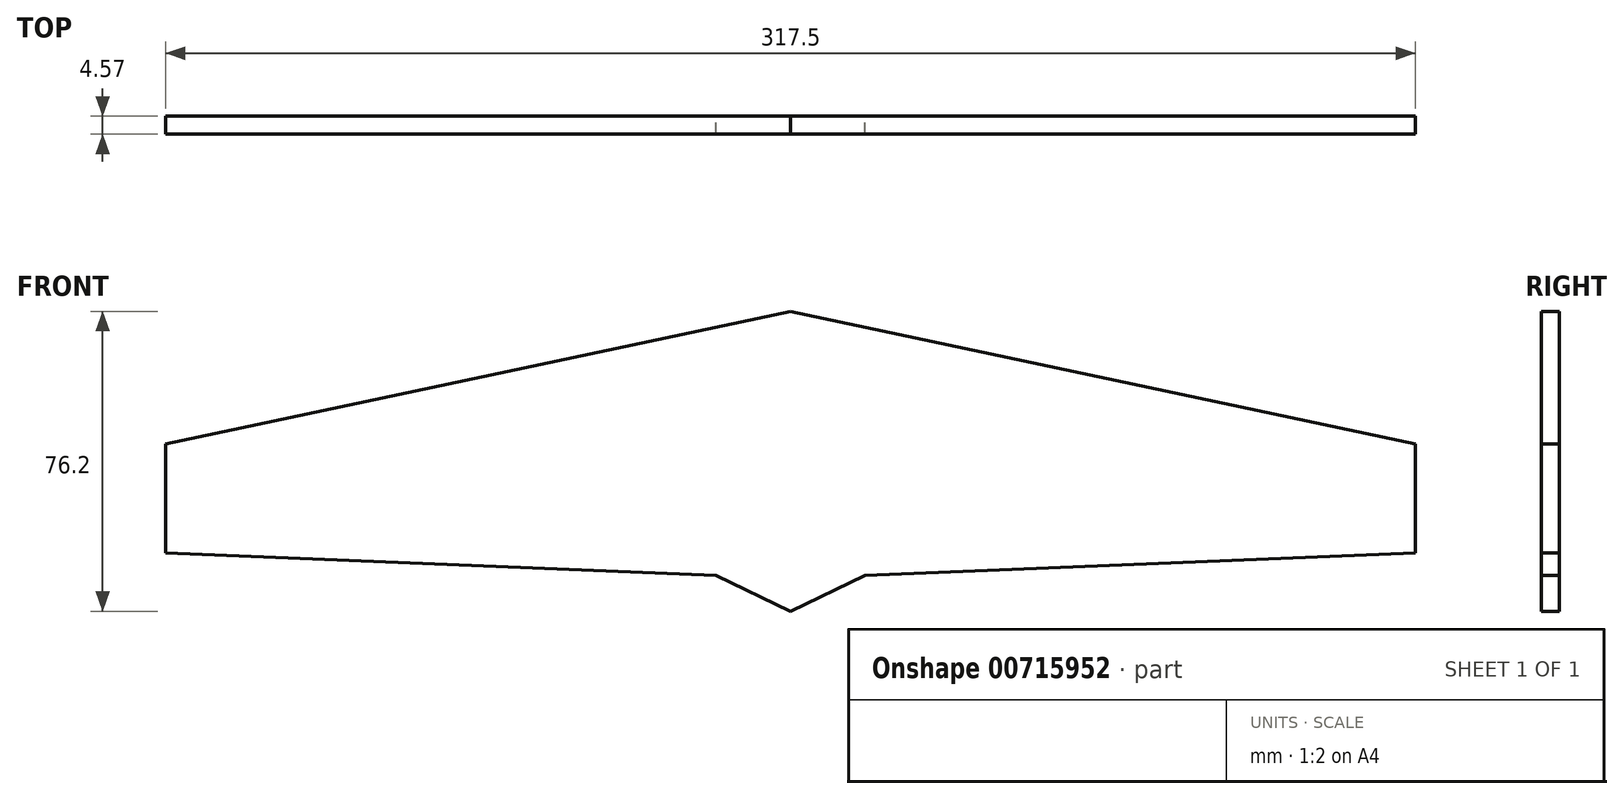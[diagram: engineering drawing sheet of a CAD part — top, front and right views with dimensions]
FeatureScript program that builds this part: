
annotation { "Feature Type Name" : "Feature", "Feature Type Description" : "" }
export const myFeature = defineFeature(function(context is Context, id is Id, definition is map)
    precondition{}
    {
        {
            var Q0;
            Q0=qCreatedBy(makeId("Front.planeOp"),FACE);
            var sketch = newSketch(context, id + "F0", { "sketchPlane" : qUnion([Q0])});
            skLineSegment(sketch, "E0.bottom", {"start": v(0, 0) * mm, "end": v(317.5, 0) * mm});
            skLineSegment(sketch, "E0.top", {"start": v(0, 76.2) * mm, "end": v(317.5, 76.2) * mm});
            skLineSegment(sketch, "E0.left", {"start": v(0, 0) * mm, "end": v(0, 76.2) * mm});
            skLineSegment(sketch, "E0.right", {"start": v(317.5, 0) * mm, "end": v(317.5, 76.2) * mm});
            skLineSegment(sketch, "E1", {"start": v(158.75, 76.2) * mm, "end": v(0, 42.45) * mm});
            skLineSegment(sketch, "E2", {"start": v(0, 42.45) * mm, "end": v(0, 14.84) * mm});
            skLineSegment(sketch, "E3", {"start": v(0, 14.84) * mm, "end": v(139.77, 9.16) * mm});
            skLineSegment(sketch, "E4", {"start": v(139.77, 9.16) * mm, "end": v(158.75, 0) * mm});
            skLineSegment(sketch, "E5", {"start": v(158.75, 0) * mm, "end": v(158.75, 76.2) * mm});
            skLineSegment(sketch, "E6.MirrorCS", {"start": v(158.75, 76.2) * mm, "end": v(317.5, 42.45) * mm});
            skLineSegment(sketch, "E7.MirrorCS", {"start": v(317.5, 42.45) * mm, "end": v(317.5, 14.84) * mm});
            skLineSegment(sketch, "E8.MirrorCS", {"start": v(317.5, 14.84) * mm, "end": v(177.73, 9.16) * mm});
            skLineSegment(sketch, "E9.MirrorCS", {"start": v(177.73, 9.16) * mm, "end": v(158.75, 0) * mm});
            skSolve(sketch);
        }
        {
            var Q0;
            Q0=makeQuery(id+"F0.imprint","IMPRINT",FACE,{"disambiguationData":[TD([[makeQuery(id+"F0.imprint","IMPRINT",EDGE,{"derivedFrom":sQuery(id+"F0.wireOp",EDGE,"E5")}),-1.0]])]});
            var Q1;
            Q1=makeQuery(id+"F0.imprint","IMPRINT",FACE,{"disambiguationData":[TD([[makeQuery(id+"F0.imprint","IMPRINT",EDGE,{"derivedFrom":sQuery(id+"F0.wireOp",EDGE,"E1")}),1.0]])]});
            extrude(context, id + "F1", {"entities" : qUnion([Q0, Q1]), "depth" : 4.57 * mm, "offsetDistance" : 25.4 * mm});
        }
    });
